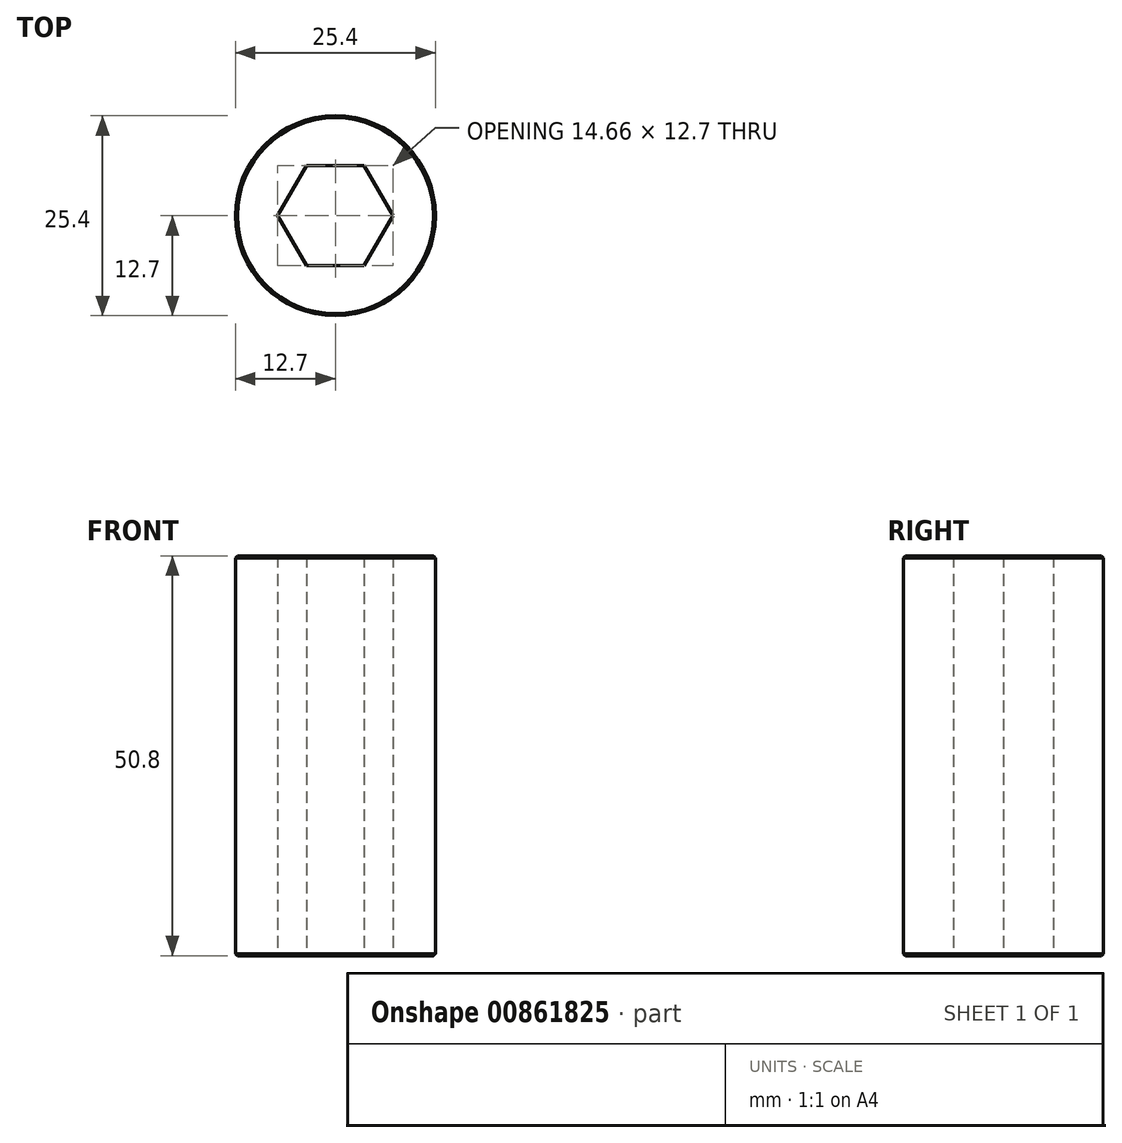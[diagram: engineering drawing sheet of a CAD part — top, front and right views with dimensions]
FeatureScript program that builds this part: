
annotation { "Feature Type Name" : "Feature", "Feature Type Description" : "" }
export const myFeature = defineFeature(function(context is Context, id is Id, definition is map)
    precondition{}
    {
        {
            var Q0;
            Q0=qCreatedBy(makeId("Top.planeOp"),FACE);
            var sketch = newSketch(context, id + "F0", { "sketchPlane" : qUnion([Q0])});
            skCircle(sketch, "E0", {"center": v(0, 0) * mm, "radius": 12.7 * mm});
            skCircle(sketch, "E1.cCircle", {"center": v(0, 0) * mm, "radius": 6.35 * mm, "construction": true});
            skLineSegment(sketch, "E1.0", {"start": v(3.67, 6.35) * mm, "end": v(7.33, 0) * mm});
            skLineSegment(sketch, "E1.1", {"start": v(7.33, 0) * mm, "end": v(3.67, -6.35) * mm});
            skLineSegment(sketch, "E1.2", {"start": v(3.67, -6.35) * mm, "end": v(-3.67, -6.35) * mm});
            skLineSegment(sketch, "E1.3", {"start": v(-3.67, -6.35) * mm, "end": v(-7.33, 0) * mm});
            skLineSegment(sketch, "E1.4", {"start": v(-7.33, 0) * mm, "end": v(-3.67, 6.35) * mm});
            skLineSegment(sketch, "E1.5", {"start": v(-3.67, 6.35) * mm, "end": v(3.67, 6.35) * mm});
            skPoint(sketch, "E1.0.midPoint", {"position": v(5.5, 3.18) * mm});
            skSolve(sketch);
        }
        {
            var Q0;
            Q0=makeQuery(id+"F0.imprint","IMPRINT",FACE,{"disambiguationData":[TD([[makeQuery(id+"F0.imprint","IMPRINT",EDGE,{"derivedFrom":sQuery(id+"F0.wireOp",EDGE,"E0")}),1.0]])]});
            extrude(context, id + "F1", {"entities" : qUnion([Q0]), "depth" : 50.8 * mm, "offsetDistance" : 25.4 * mm});
        }
        {
            var Q0;
            Q0=makeQuery(id+"F1.opExtrude","CAP_EDGE",EDGE,{"disambiguationData":[OSD([sQuery(id+"F0.wireOp",EDGE,"E0")])],"isStart":false});
            var Q1;
            Q1=makeQuery(id+"F1.opExtrude","CAP_EDGE",EDGE,{"disambiguationData":[OSD([sQuery(id+"F0.wireOp",EDGE,"E0")])],"isStart":true});
            chamfer(context, id + "F2", {"entities" : qUnion([Q0, Q1]), "width" : 0.25 * mm, "tangentPropagation" : true});
        }
    });
